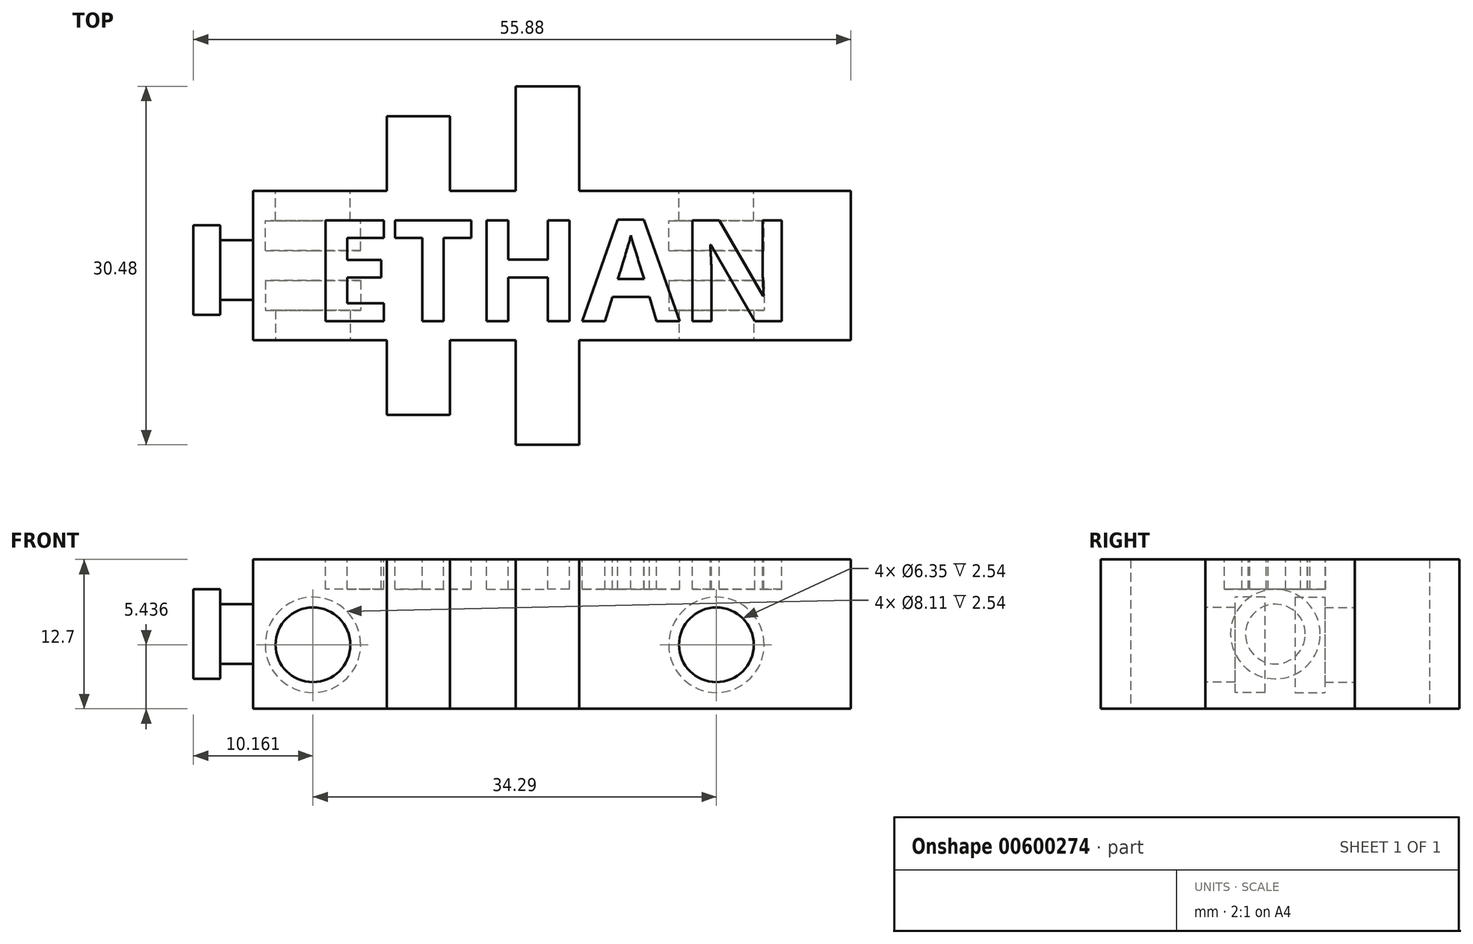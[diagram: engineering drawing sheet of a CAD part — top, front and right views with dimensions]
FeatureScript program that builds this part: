
annotation { "Feature Type Name" : "Feature", "Feature Type Description" : "" }
export const myFeature = defineFeature(function(context is Context, id is Id, definition is map)
    precondition{}
    {
        {
            var Q0;
            Q0=qCreatedBy(makeId("Top.planeOp"),FACE);
            var sketch = newSketch(context, id + "F0", { "sketchPlane" : qUnion([Q0])});
            skLineSegment(sketch, "E0.left", {"start": v(-27.15, 6.74) * mm, "end": v(-27.15, -5.96) * mm});
            skLineSegment(sketch, "E0.right", {"start": v(23.65, 6.74) * mm, "end": v(23.65, -5.96) * mm});
            skLineSegment(sketch, "E1", {"start": v(-27.15, -5.96) * mm, "end": v(23.65, -5.96) * mm});
            skLineSegment(sketch, "E2", {"start": v(-27.15, 6.74) * mm, "end": v(23.65, 6.74) * mm});
            skLineSegment(sketch, "E3.bottom", {"start": v(-4.83, 15.63) * mm, "end": v(0.55, 15.63) * mm});
            skLineSegment(sketch, "E3.top", {"start": v(-4.83, -14.85) * mm, "end": v(0.55, -14.85) * mm});
            skLineSegment(sketch, "E3.left", {"start": v(-4.83, 15.63) * mm, "end": v(-4.83, -14.85) * mm});
            skLineSegment(sketch, "E3.right", {"start": v(0.55, 15.63) * mm, "end": v(0.55, -14.85) * mm});
            skLineSegment(sketch, "E4.bottom", {"start": v(-15.8, 13.1) * mm, "end": v(-10.43, 13.1) * mm});
            skLineSegment(sketch, "E4.top", {"start": v(-15.8, -12.3) * mm, "end": v(-10.43, -12.3) * mm});
            skLineSegment(sketch, "E4.left", {"start": v(-15.8, 13.1) * mm, "end": v(-15.8, -12.3) * mm});
            skLineSegment(sketch, "E4.right", {"start": v(-10.43, 13.1) * mm, "end": v(-10.43, -12.3) * mm});
            skSolve(sketch);
        }
        {
            var Q0;
            Q0=qSketchRegion(id+"F0",true);
            extrude(context, id + "F1", {"entities" : qUnion([Q0]), "depth" : 12.7 * mm, "offsetDistance" : 25.4 * mm});
        }
        {
            var Q0;
            Q0=makeQuery(id+"F1.opExtrude","CAP_FACE",FACE,{"disambiguationData":[OSD([sQuery(id+"F0.wireOp",EDGE,"E0.bottom"),sQuery(id+"F0.wireOp",EDGE,"E0.top"),sQuery(id+"F0.wireOp",EDGE,"E0.left"),sQuery(id+"F0.wireOp",EDGE,"E0.right")])],"isStart":false});
            var sketch = newSketch(context, id + "F2", { "sketchPlane" : qUnion([Q0])});
            skText(sketch, "E5", { "text": "ETHAN", "fontName": "OpenSans-Bold.ttf"});
            skLineSegment(sketch, "E6", {"start": v(-27.15, 1.62) * mm, "end": v(-22.07, 1.62) * mm, "construction": true});
            skLineSegment(sketch, "E7", {"start": v(18.57, 1.82) * mm, "end": v(23.65, 1.82) * mm, "construction": true});
            skLineSegment(sketch, "E8", {"start": v(-7.63, 6.74) * mm, "end": v(-7.63, 4.72) * mm, "construction": true});
            skLineSegment(sketch, "E9", {"start": v(-7.63, -3.93) * mm, "end": v(-7.63, -5.96) * mm, "construction": true});
            const initialGuessF2  = {"E5": [-0.02207, -0.00433, 1, 0, 0.00865]};
            skSetInitialGuess(sketch, initialGuessF2);
            skSolve(sketch);
        }
        {
            var Q0;
            Q0=qSketchRegion(id+"F2",true);
            extrude(context, id + "F3", {"entities" : qUnion([Q0]), "operationType" : NewBodyOperationType.REMOVE, "oppositeDirection" : true, "depth" : 2.54 * mm, "offsetDistance" : 25.4 * mm});
        }
        {
            var Q0;
            {var subQ0=sQuery(id+"F0.wireOp",EDGE,"E2");Q0=makeQuery(id+"F1.opExtrude","SWEPT_FACE",FACE,{"disambiguationData":[OSD([subQ0]),TDD([makeQuery(id+"F0.imprint","IMPRINT",EDGE,{"disambiguationData":[TD([[makeQuery(id+"F0.imprint","INTERSECT",VERTEX,{"derivedFrom":[sQuery(id+"F0.wireOp",EDGE,"E0.left"),subQ0]}),-1.0]])],"derivedFrom":subQ0})])]});}
            var sketch = newSketch(context, id + "F4", { "sketchPlane" : qUnion([Q0])});
            skCircle(sketch, "E10", {"center": v(22.07, 5.44) * mm, "radius": 3.18 * mm});
            skCircle(sketch, "E11", {"center": v(-12.22, 5.44) * mm, "radius": 3.18 * mm});
            skSolve(sketch);
        }
        {
            var Q0;
            Q0 = qSketchRegion(id + "F4", true);
            extrude(context, id + "F5", {"entities" : qUnion([Q0]), "operationType" : NewBodyOperationType.REMOVE, "oppositeDirection" : true, "depth" : 2.54 * mm, "offsetDistance" : 25.4 * mm});
        }
        {
            var Q0;
            Q0=makeQuery(id+"F5.boolean.opBoolean","COPY",FACE,{"derivedFrom":makeQuery(id+"F5.opExtrude","CAP_FACE",FACE,{"disambiguationData":[OSD([sQuery(id+"F4.wireOp",EDGE,"E11")])],"isStart":false})});
            var sketch = newSketch(context, id + "F6", { "sketchPlane" : qUnion([Q0])});
            skCircle(sketch, "E12", {"center": v(-12.22, 5.44) * mm, "radius": 4.05 * mm});
            skCircle(sketch, "E13", {"center": v(22.07, 5.44) * mm, "radius": 4.05 * mm});
            skSolve(sketch);
        }
        {
            var Q0;
            Q0 = qSketchRegion(id + "F6", true);
            extrude(context, id + "F7", {"entities" : qUnion([Q0]), "operationType" : NewBodyOperationType.REMOVE, "oppositeDirection" : true, "depth" : 2.54 * mm, "offsetDistance" : 25.4 * mm});
        }
        {
            var Q0;
            {var subQ0=sQuery(id+"F0.wireOp",EDGE,"E1");Q0=makeQuery(id+"F1.opExtrude","SWEPT_FACE",FACE,{"disambiguationData":[OSD([subQ0]),TDD([makeQuery(id+"F0.imprint","IMPRINT",EDGE,{"disambiguationData":[TD([[makeQuery(id+"F0.imprint","INTERSECT",VERTEX,{"derivedFrom":[sQuery(id+"F0.wireOp",EDGE,"E0.right"),subQ0]}),1.0]])],"derivedFrom":subQ0})])]});}
            var sketch = newSketch(context, id + "F8", { "sketchPlane" : qUnion([Q0])});
            skCircle(sketch, "E14", {"center": v(-22.07, 5.44) * mm, "radius": 3.18 * mm});
            skCircle(sketch, "E15", {"center": v(12.22, 5.44) * mm, "radius": 3.18 * mm});
            skSolve(sketch);
        }
        {
            var Q0;
            Q0 = qSketchRegion(id + "F8", true);
            extrude(context, id + "F9", {"entities" : qUnion([Q0]), "operationType" : NewBodyOperationType.REMOVE, "oppositeDirection" : true, "depth" : 2.54 * mm, "offsetDistance" : 25.4 * mm});
        }
        {
            var Q0;
            Q0=makeQuery(id+"F9.boolean.opBoolean","COPY",FACE,{"derivedFrom":makeQuery(id+"F9.opExtrude","CAP_FACE",FACE,{"disambiguationData":[OSD([sQuery(id+"F8.wireOp",EDGE,"E14")])],"isStart":false})});
            var sketch = newSketch(context, id + "F10", { "sketchPlane" : qUnion([Q0])});
            skCircle(sketch, "E16", {"center": v(-22.07, 5.44) * mm, "radius": 4.05 * mm});
            skCircle(sketch, "E17", {"center": v(12.22, 5.44) * mm, "radius": 4.05 * mm});
            skSolve(sketch);
        }
        {
            var Q0;
            Q0 = qSketchRegion(id + "F10", true);
            extrude(context, id + "F11", {"entities" : qUnion([Q0]), "operationType" : NewBodyOperationType.REMOVE, "oppositeDirection" : true, "depth" : 2.54 * mm, "offsetDistance" : 25.4 * mm});
        }
        {
            var Q0;
            Q0=makeQuery(id+"F1.opExtrude","SWEPT_FACE",FACE,{"disambiguationData":[OSD([sQuery(id+"F0.wireOp",EDGE,"E0.left")])]});
            var sketch = newSketch(context, id + "F12", { "sketchPlane" : qUnion([Q0])});
            skCircle(sketch, "E18", {"center": v(0, 6.35) * mm, "radius": 2.54 * mm});
            skSolve(sketch);
        }
        {
            var Q0;
            Q0 = qSketchRegion(id + "F12", true);
            extrude(context, id + "F13", {"entities" : qUnion([Q0]), "operationType" : NewBodyOperationType.ADD, "depth" : 2.8 * mm, "offsetDistance" : 25.4 * mm});
        }
        {
            var Q0;
            Q0=makeQuery(id+"F13.opExtrude","CAP_FACE",FACE,{"disambiguationData":[OSD([sQuery(id+"F12.wireOp",EDGE,"E18")])],"isStart":false});
            var sketch = newSketch(context, id + "F14", { "sketchPlane" : qUnion([Q0])});
            skCircle(sketch, "E19", {"center": v(0, 6.35) * mm, "radius": 3.8 * mm});
            skSolve(sketch);
        }
        {
            var Q0;
            Q0 = qSketchRegion(id + "F14", true);
            extrude(context, id + "F15", {"entities" : qUnion([Q0]), "operationType" : NewBodyOperationType.ADD, "depth" : 2.3 * mm, "offsetDistance" : 25.4 * mm});
        }
        {
            var Q0;
            Q0=qSketchRegion(id+"F2",true);
            extrude(context, id + "F16", {"entities" : qUnion([Q0]), "operationType" : NewBodyOperationType.REMOVE, "depth" : 2.54 * mm, "offsetDistance" : 25.4 * mm});
        }
    });
